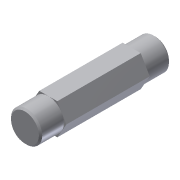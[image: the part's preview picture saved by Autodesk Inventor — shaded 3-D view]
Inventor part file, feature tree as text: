
AUTODESK INVENTOR PART (.ipt)
format: ipt  version: 2013 (Build 170138000, 138)  size: 87,552 bytes
history: native  units: in
note: dims shown in document units (in); Inventor stores cm internally (conversion verified against a paired STEP export)
features: chamfer x1, other x1, imported_body x1
ambient origin geometry x8: Origin, YZ Plane, XZ Plane, XY Plane, X Axis, Y Axis, Z Axis, Center Point
feature tree (3):
  chamfer  "Chamfer1"  [1 undecoded]
  other  "217-2454-003 Rev11"
  imported_body  "Base1"
note: 1 required parameter value undecoded (feature->parameter linkage not recoverable at this tier; creation-order binding heuristic only, values carry confidence <= 0.55)
